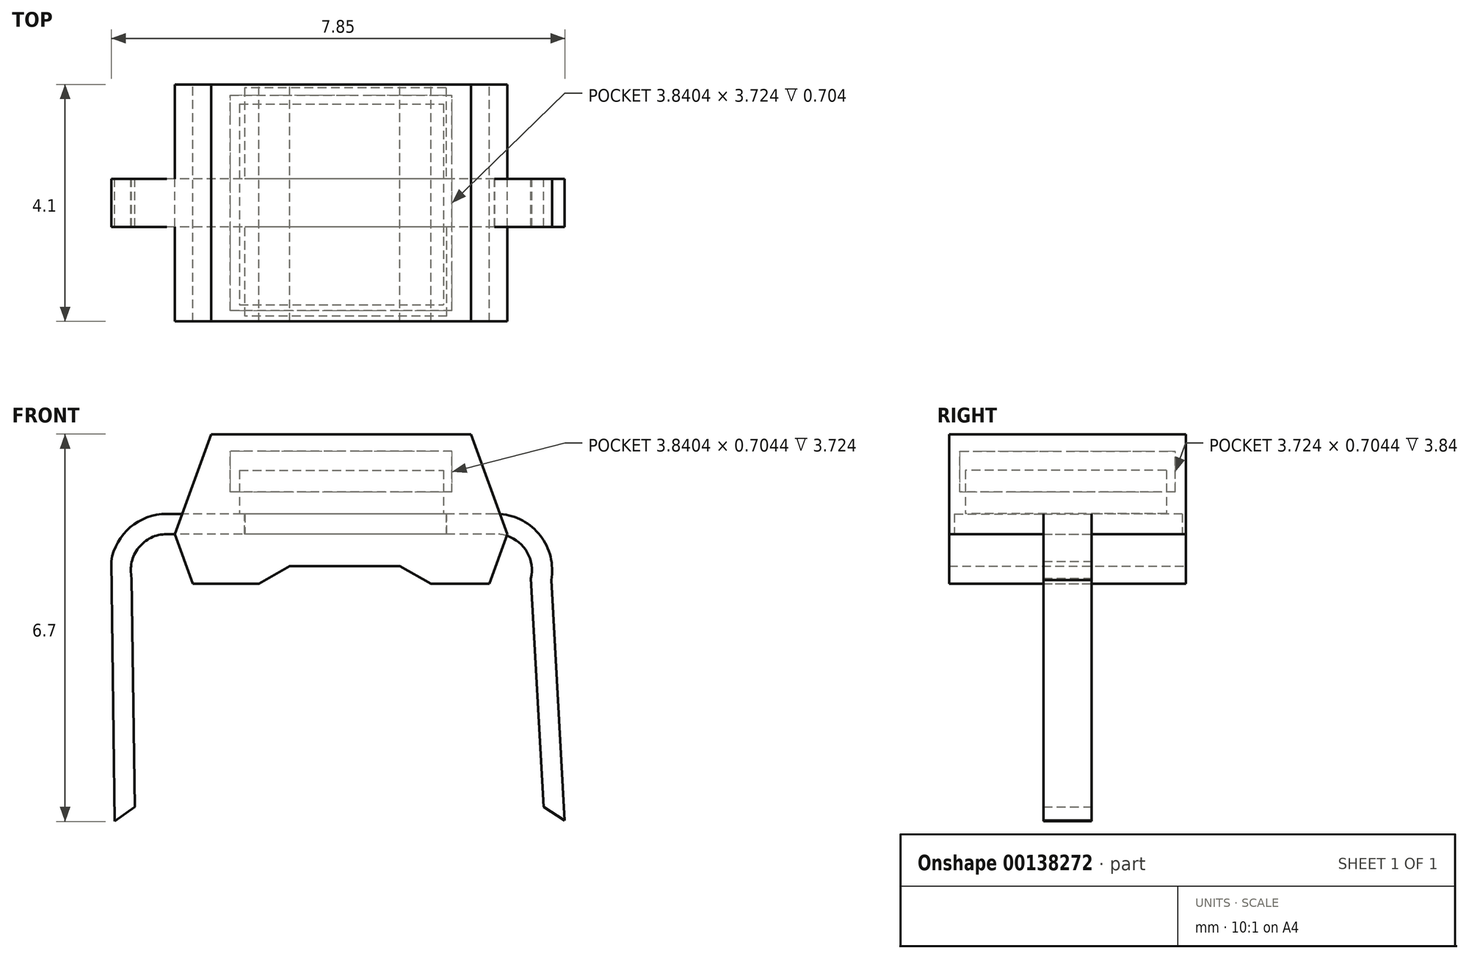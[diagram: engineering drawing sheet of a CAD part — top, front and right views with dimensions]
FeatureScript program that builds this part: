
annotation { "Feature Type Name" : "Feature", "Feature Type Description" : "" }
export const myFeature = defineFeature(function(context is Context, id is Id, definition is map)
    precondition{}
    {
        {
            var Q0;
            Q0=qCreatedBy(makeId("Front.planeOp"),FACE);
            var sketch = newSketch(context, id + "F0", { "sketchPlane" : qUnion([Q0])});
            skLineSegment(sketch, "E0", {"start": v(-2.31, 1.73) * mm, "end": v(2.19, 1.73) * mm});
            skLineSegment(sketch, "E1", {"start": v(2.19, 1.73) * mm, "end": v(2.81, 0) * mm});
            skLineSegment(sketch, "E2", {"start": v(2.81, 0) * mm, "end": v(2.5, -0.86) * mm});
            skLineSegment(sketch, "E3", {"start": v(2.5, -0.86) * mm, "end": v(1.49, -0.86) * mm});
            skLineSegment(sketch, "E4", {"start": v(1.49, -0.86) * mm, "end": v(0.95, -0.55) * mm});
            skLineSegment(sketch, "E5", {"start": v(-0.95, -0.55) * mm, "end": v(-1.49, -0.86) * mm});
            skLineSegment(sketch, "E6", {"start": v(-1.49, -0.86) * mm, "end": v(-2.63, -0.86) * mm});
            skLineSegment(sketch, "E7", {"start": v(-2.63, -0.86) * mm, "end": v(-2.94, 0) * mm});
            skLineSegment(sketch, "E8", {"start": v(-2.94, 0) * mm, "end": v(-2.31, 1.73) * mm});
            skLineSegment(sketch, "E9", {"start": v(-0.95, -0.55) * mm, "end": v(0.95, -0.55) * mm});
            skSolve(sketch);
        }
        {
            var Q0;
            Q0 = qSketchRegion(id + "F0", true);
            extrude(context, id + "F1", {"entities" : qUnion([Q0]), "endBound" : BoundingType.SYMMETRIC, "depth" : 4.1 * mm});
        }
        {
            var Q0;
            Q0=qCreatedBy(makeId("Front.planeOp"),FACE);
            var sketch = newSketch(context, id + "F2", { "sketchPlane" : qUnion([Q0])});
            skArc(sketch, "E10", {"start": v(3.22, -0.77) * mm, "mid": v(3.1, -0.23) * mm, "end": v(2.6, 0) * mm});
            skLineSegment(sketch, "E11", {"start": v(3.22, -0.77) * mm, "end": v(3.44, -4.72) * mm});
            skLineSegment(sketch, "E12", {"start": v(2.6, 0) * mm, "end": v(-3.08, 0) * mm});
            skArc(sketch, "E13", {"start": v(-3.08, 0) * mm, "mid": v(-3.57, -0.23) * mm, "end": v(-3.69, -0.76) * mm});
            skLineSegment(sketch, "E14", {"start": v(-3.69, -0.76) * mm, "end": v(-3.63, -4.72) * mm});
            skLineSegment(sketch, "E15.0", {"start": v(-4.04, -0.47) * mm, "end": v(-3.98, -4.97) * mm});
            skLineSegment(sketch, "E15.1", {"start": v(3.57, -0.8) * mm, "end": v(3.8, -4.95) * mm});
            skArc(sketch, "E15.2", {"start": v(3.57, -0.8) * mm, "mid": v(3.35, 0.01) * mm, "end": v(2.59, 0.35) * mm});
            skLineSegment(sketch, "E15.3", {"start": v(2.59, 0.35) * mm, "end": v(-3.08, 0.35) * mm});
            skArc(sketch, "E15.4", {"start": v(-3.08, 0.35) * mm, "mid": v(-3.71, 0.12) * mm, "end": v(-4.04, -0.47) * mm});
            skLineSegment(sketch, "E16", {"start": v(-3.98, -4.97) * mm, "end": v(-3.63, -4.72) * mm});
            skLineSegment(sketch, "E17", {"start": v(3.44, -4.72) * mm, "end": v(3.8, -4.95) * mm});
            skLineSegment(sketch, "E18", {"start": v(2.59, 0.35) * mm, "end": v(2.6, 0) * mm});
            skLineSegment(sketch, "E19", {"start": v(-3.08, 0.35) * mm, "end": v(-3.08, 0) * mm});
            skSolve(sketch);
        }
        {
            var Q0;
            Q0 = qSketchRegion(id + "F2", true);
            extrude(context, id + "F3", {"entities" : qUnion([Q0]), "endBound" : BoundingType.SYMMETRIC, "depth" : .83 * mm});
        }
        {
            var Q0;
            Q0=makeQuery(id+"F1.opExtrude","SWEPT_FACE",FACE,{"disambiguationData":[OSD([sQuery(id+"F0.wireOp",EDGE,"E0")])]});
            var sketch = newSketch(context, id + "F4", { "sketchPlane" : qUnion([Q0])});
            skLineSegment(sketch, "E20", {"start": v(-0.06, 2.05) * mm, "end": v(-0.06, -2.05) * mm, "construction": true});
            skLineSegment(sketch, "E21", {"start": v(-2.31, 0) * mm, "end": v(2.19, 0) * mm, "construction": true});
            skLineSegment(sketch, "E22.bottom", {"start": v(1.86, 1.86) * mm, "end": v(-1.98, 1.86) * mm});
            skLineSegment(sketch, "E22.top", {"start": v(1.86, -1.86) * mm, "end": v(-1.98, -1.86) * mm});
            skLineSegment(sketch, "E22.left", {"start": v(1.86, 1.86) * mm, "end": v(1.86, -1.86) * mm});
            skLineSegment(sketch, "E22.right", {"start": v(-1.98, 1.86) * mm, "end": v(-1.98, -1.86) * mm});
            skPoint(sketch, "E22.middle", {"position": v(-0.06, 0) * mm});
            skSolve(sketch);
        }
        {
            var Q0;
            Q0 = qSketchRegion(id + "F4", true);
            extrude(context, id + "F5", {"entities" : qUnion([Q0]), "operationType" : NewBodyOperationType.REMOVE, "oppositeDirection" : true, "depth" : 1 * mm});
        }
        {
            var Q0;
            Q0=makeQuery(id+"F3.opExtrude","CAP_FACE",FACE,{"disambiguationData":[OSD([sQuery(id+"F2.wireOp",EDGE,"E10"),sQuery(id+"F2.wireOp",EDGE,"E11"),sQuery(id+"F2.wireOp",EDGE,"E12"),sQuery(id+"F2.wireOp",EDGE,"E13"),sQuery(id+"F2.wireOp",EDGE,"E14"),sQuery(id+"F2.wireOp",EDGE,"E15.0"),sQuery(id+"F2.wireOp",EDGE,"E15.1"),sQuery(id+"F2.wireOp",EDGE,"E15.2"),sQuery(id+"F2.wireOp",EDGE,"E15.3"),sQuery(id+"F2.wireOp",EDGE,"E15.4"),sQuery(id+"F2.wireOp",EDGE,"E16"),sQuery(id+"F2.wireOp",EDGE,"E17")])],"isStart":true});
            var sketch = newSketch(context, id + "F6", { "sketchPlane" : qUnion([Q0])});
            skLineSegment(sketch, "E23", {"start": v(-1.75, 0.35) * mm, "end": v(-1.75, 0) * mm});
            skLineSegment(sketch, "E24", {"start": v(-1.75, 0) * mm, "end": v(1.74, 0) * mm});
            skLineSegment(sketch, "E25", {"start": v(1.74, 0) * mm, "end": v(1.74, 0.35) * mm});
            skLineSegment(sketch, "E26", {"start": v(1.74, 0.35) * mm, "end": v(-1.75, 0.35) * mm});
            skLineSegment(sketch, "E27", {"start": v(1.74, 0.35) * mm, "end": v(1.74, 0) * mm});
            skLineSegment(sketch, "E28", {"start": v(-1.75, 0) * mm, "end": v(-1.75, 0.35) * mm});
            skSolve(sketch);
        }
        {
            var Q0;
            Q0 = qSketchRegion(id + "F6", true);
            extrude(context, id + "F7", {"entities" : qUnion([Q0]), "depth" : 1.57 * mm});
        }
        {
            var Q0;
            Q0=makeQuery(id+"F3.opExtrude","CAP_FACE",FACE,{"disambiguationData":[OSD([sQuery(id+"F2.wireOp",EDGE,"E10"),sQuery(id+"F2.wireOp",EDGE,"E11"),sQuery(id+"F2.wireOp",EDGE,"E12"),sQuery(id+"F2.wireOp",EDGE,"E13"),sQuery(id+"F2.wireOp",EDGE,"E14"),sQuery(id+"F2.wireOp",EDGE,"E15.0"),sQuery(id+"F2.wireOp",EDGE,"E15.1"),sQuery(id+"F2.wireOp",EDGE,"E15.2"),sQuery(id+"F2.wireOp",EDGE,"E15.3"),sQuery(id+"F2.wireOp",EDGE,"E15.4"),sQuery(id+"F2.wireOp",EDGE,"E16"),sQuery(id+"F2.wireOp",EDGE,"E17")])],"isStart":false});
            var sketch = newSketch(context, id + "F8", { "sketchPlane" : qUnion([Q0])});
            skLineSegment(sketch, "E29", {"start": v(-1.73, 0.35) * mm, "end": v(-1.73, 0) * mm});
            skLineSegment(sketch, "E30", {"start": v(-1.73, 0) * mm, "end": v(1.77, 0) * mm});
            skLineSegment(sketch, "E31", {"start": v(1.77, 0) * mm, "end": v(1.77, 0.35) * mm});
            skLineSegment(sketch, "E32", {"start": v(1.77, 0.35) * mm, "end": v(-1.73, 0.35) * mm});
            skSolve(sketch);
        }
        {
            var Q0;
            Q0 = qSketchRegion(id + "F8", true);
            extrude(context, id + "F9", {"entities" : qUnion([Q0]), "depth" : 1.54 * mm});
        }
        {
            var Q0;
            Q0=makeQuery(id+"F5.boolean.opBoolean","COPY",FACE,{"derivedFrom":makeQuery(id+"F5.opExtrude","CAP_FACE",FACE,{"disambiguationData":[OSD([sQuery(id+"F4.wireOp",EDGE,"E22.bottom"),sQuery(id+"F4.wireOp",EDGE,"E22.top"),sQuery(id+"F4.wireOp",EDGE,"E22.left"),sQuery(id+"F4.wireOp",EDGE,"E22.right")])],"isStart":false})});
            var sketch = newSketch(context, id + "F10", { "sketchPlane" : qUnion([Q0])});
            skLineSegment(sketch, "E33.bottom", {"start": v(-1.82, 1.71) * mm, "end": v(1.7, 1.71) * mm});
            skLineSegment(sketch, "E33.top", {"start": v(-1.82, -1.76) * mm, "end": v(1.7, -1.76) * mm});
            skLineSegment(sketch, "E33.left", {"start": v(-1.82, 1.71) * mm, "end": v(-1.82, -1.76) * mm});
            skLineSegment(sketch, "E33.right", {"start": v(1.7, 1.71) * mm, "end": v(1.7, -1.76) * mm});
            skSolve(sketch);
        }
        {
            var Q0;
            Q0 = qSketchRegion(id + "F10", true);
            extrude(context, id + "F11", {"entities" : qUnion([Q0]), "endBound" : BoundingType.SYMMETRIC, "depth" : 0.75 * mm});
        }
        {
            var Q0;
            Q0=makeQuery(id+"F5.boolean.opBoolean","COPY",FACE,{"derivedFrom":makeQuery(id+"F5.opExtrude","SWEPT_FACE",FACE,{"disambiguationData":[OSD([sQuery(id+"F4.wireOp",EDGE,"E22.bottom")])]})});
            var sketch = newSketch(context, id + "F12", { "sketchPlane" : qUnion([Q0])});
            skLineSegment(sketch, "E34.bottom", {"start": v(-1.98, 1.73) * mm, "end": v(1.86, 1.73) * mm});
            skLineSegment(sketch, "E34.top", {"start": v(-1.98, 1.43) * mm, "end": v(1.86, 1.43) * mm});
            skLineSegment(sketch, "E34.left", {"start": v(-1.98, 1.73) * mm, "end": v(-1.98, 1.43) * mm});
            skLineSegment(sketch, "E34.right", {"start": v(1.86, 1.73) * mm, "end": v(1.86, 1.43) * mm});
            skSolve(sketch);
        }
        {
            var Q0;
            Q0 = qSketchRegion(id + "F12", true);
            var Q1;
            Q1=makeQuery(id+"F5.boolean.opBoolean","COPY",FACE,{"derivedFrom":makeQuery(id+"F5.opExtrude","SWEPT_FACE",FACE,{"disambiguationData":[OSD([sQuery(id+"F4.wireOp",EDGE,"E22.top")])]})});
            extrude(context, id + "F13", {"entities" : qUnion([Q0]), "operationType" : NewBodyOperationType.ADD, "endBound" : BoundingType.UP_TO_SURFACE, "endBoundEntityFace" : qUnion([Q1]), "depth" : 25 * mm});
        }
    });
